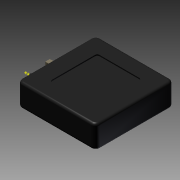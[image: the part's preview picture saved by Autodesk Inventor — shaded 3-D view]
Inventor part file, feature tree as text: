
AUTODESK INVENTOR PART (.ipt)
format: ipt  version: 2011 (Build 150239000, 239)  size: 168,448 bytes
history: native  units: mm
features: plane x4, sketch x4, other x4, extrude x3, draft x2, imported_body x1
ambient origin geometry x8: Origin, YZ Plane, XZ Plane, XY Plane, X Axis, Y Axis, Z Axis, Center Point
bodies: Solid1 (feature_tree)
feature tree (18):
  imported_body  "Base1"
  plane  "Work Plane2"
  extrude  "Extrusion1"  Depth=3.175mm
  draft  "FaceDraft1"
  extrude  "Extrusion2"  Depth=12.7mm
  extrude  "Extrusion3"  Depth=0.436332mm
  draft  "FaceDraft2"
  sketch  "Sketch6"  dims[d7=4.7625mm d8=6.35mm d9=0.0mm d10=3.175mm d11=0.0mm d12=0.872665mm d13=3.175mm d14=6.35mm]
  other  "Work Point2"
  other  "Work Point3"
  plane  "Work Plane1"
  sketch  "Sketch1"  dims[d0=6.35mm d1=3.175mm]
  sketch  "Sketch2"  dims[d2=6.35mm d3=12.7mm]
  sketch  "Sketch5"  dims[d4=12.7mm d5=0.0mm d6=0.436332mm]
  plane  "Work Plane3"
  other  "Work Axis1"
  plane  "Work Plane4"
  other  "Work Axis2"
